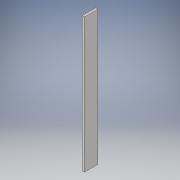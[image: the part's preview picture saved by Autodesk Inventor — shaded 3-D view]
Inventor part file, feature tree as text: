
AUTODESK INVENTOR PART (.ipt)
format: ipt  version: 2017 (Build 210142000, 142)  size: 91,136 bytes
history: native  units: in
note: dims shown in document units (in); Inventor stores cm internally (conversion verified against a paired STEP export)
features: extrude x1, sketch x1
ambient origin geometry x8: Origin, YZ Plane, XZ Plane, XY Plane, X Axis, Y Axis, Z Axis, Center Point
bodies: Solid1 (feature_tree)
feature tree (2):
  extrude  "Extrusion1"  Depth=6.0in
  sketch  "Sketch1"  dims[d0=1.0in d1=6.0in d2=59.0in d3=0.0in]
